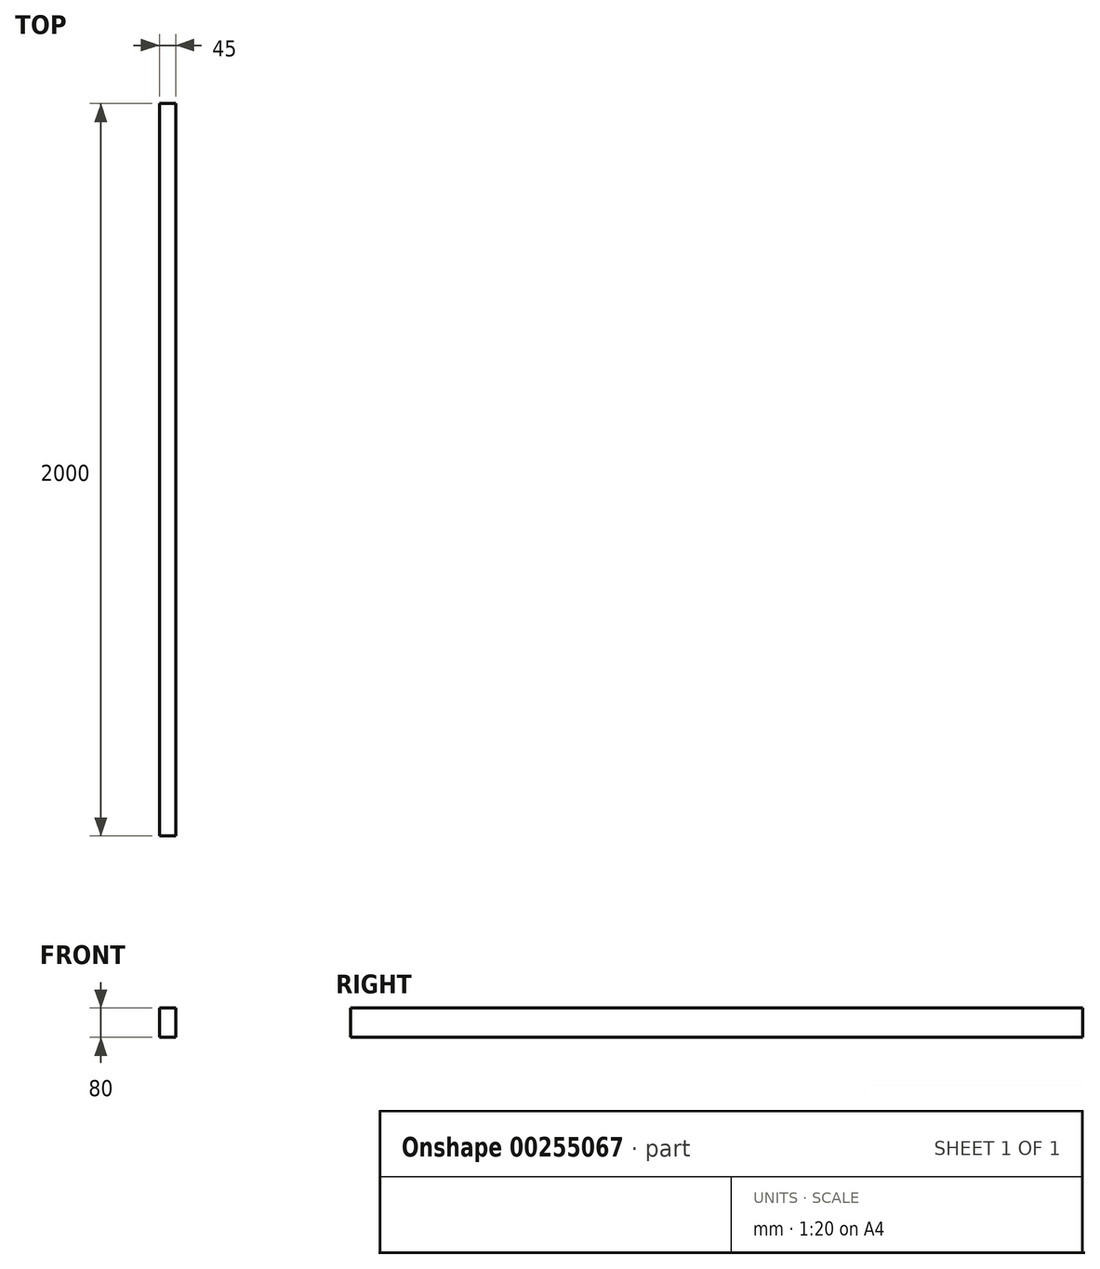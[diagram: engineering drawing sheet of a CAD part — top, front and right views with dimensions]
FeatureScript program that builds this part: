
annotation { "Feature Type Name" : "Feature", "Feature Type Description" : "" }
export const myFeature = defineFeature(function(context is Context, id is Id, definition is map)
    precondition{}
    {
        {
            var Q0;
            Q0=qCreatedBy(makeId("Front.planeOp"),FACE);
            var sketch = newSketch(context, id + "F0", { "sketchPlane" : qUnion([Q0])});
            skLineSegment(sketch, "E0.bottom", {"start": v(45, -40) * mm, "end": v(-45, -40) * mm});
            skLineSegment(sketch, "E0.top", {"start": v(45, 40) * mm, "end": v(-45, 40) * mm});
            skLineSegment(sketch, "E0.left", {"start": v(45, -40) * mm, "end": v(45, 40) * mm});
            skLineSegment(sketch, "E0.right", {"start": v(-45, -40) * mm, "end": v(-45, 40) * mm});
            skPoint(sketch, "E0.middle", {"position": v(0, 0) * mm});
            skLineSegment(sketch, "E1", {"start": v(0, 40) * mm, "end": v(0, -40) * mm});
            skSolve(sketch);
        }
        {
            var Q0;
            {var subQ0=sQuery(id+"F0.wireOp",EDGE,"E0.right");Q0=makeQuery(id+"F0.imprint","IMPRINT",FACE,{"disambiguationData":[TD([[makeQuery(id+"F0.imprint","IMPRINT",EDGE,{"derivedFrom":subQ0}),-1.0]])]});}
            extrude(context, id + "F1", {"entities" : qUnion([Q0]), "depth" : 2000 * mm});
        }
    });
